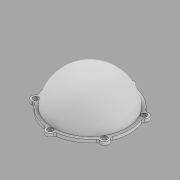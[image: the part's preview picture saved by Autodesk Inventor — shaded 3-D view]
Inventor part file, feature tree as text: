
AUTODESK INVENTOR PART (.ipt)
format: ipt  version: 2020 (Build 240168000, 168)  size: 199,680 bytes
history: native  units: mm
features: sketch x5, extrude x2, other x1, hole x1, revolve x1
ambient origin geometry x8: Origin, YZ Plane, XZ Plane, XY Plane, X Axis, Y Axis, Z Axis, Center Point
bodies: Body1 (feature_tree), Body2 (feature_tree)
feature tree (10):
  other  "Sólido1"
  extrude  "Extrusión1"  Depth=0.3mm TaperAngle=0.0deg
  extrude  "Extrusión2"  Depth=1.0mm
  hole  "Agujero1"  [1 undecoded]
  sketch  "Boceto4"  dims[d13=4.0mm d14=4.0mm]
  revolve  "Revolución1"  [1 undecoded]
  sketch  "Boceto1"  dims[d0=33.0mm d1=0.3mm d2=0.0mm]
  sketch  "Boceto2"  dims[d4=4.0mm d10=1.0mm]
  sketch  "Boceto3"  dims[d11=4.0mm d12=4.0mm]
  sketch  "Boceto5"  dims[d15=4.0mm d16=1.0mm d17=32.0mm d18=1.5mm d19=0.0mm d20=1.562mm d21=9.652mm d22=2.5mm d23=0.3mm d24=90.0deg d25=14.9352mm d26=0.0mm d27=34.0mm d28=180.0deg d29=180.0deg]
note: 2 required parameter values undecoded (feature->parameter linkage not recoverable at this tier; creation-order binding heuristic only, values carry confidence <= 0.55)